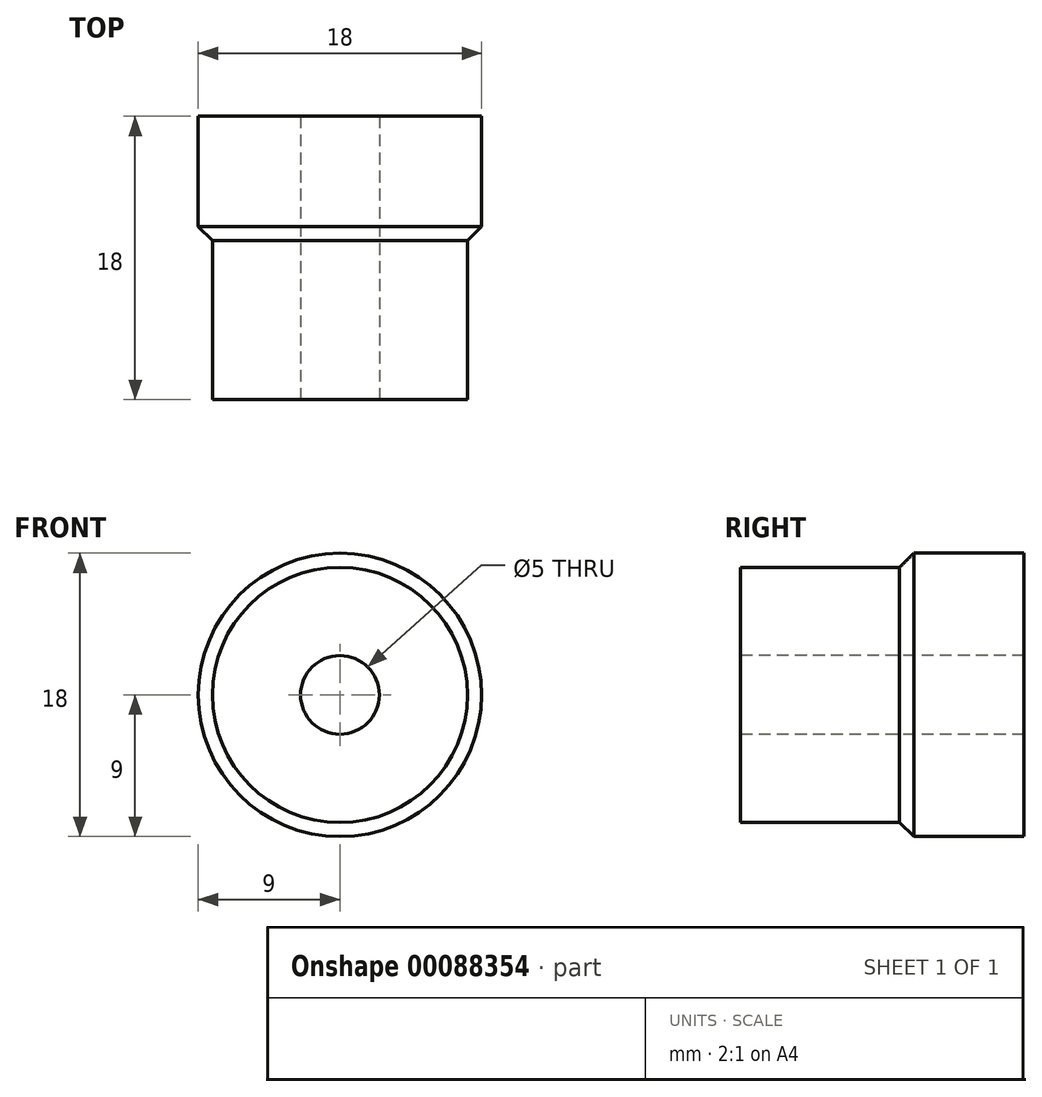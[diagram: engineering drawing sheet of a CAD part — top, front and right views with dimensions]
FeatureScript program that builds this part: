
annotation { "Feature Type Name" : "Feature", "Feature Type Description" : "" }
export const myFeature = defineFeature(function(context is Context, id is Id, definition is map)
    precondition{}
    {
        {
            var Q0;
            Q0=qCreatedBy(makeId("Front.planeOp"),FACE);
            var sketch = newSketch(context, id + "F0", { "sketchPlane" : qUnion([Q0])});
            skCircle(sketch, "E0", {"center": v(0, 0) * mm, "radius": 9 * mm});
            skSolve(sketch);
        }
        {
            var Q0;
            Q0 = qSketchRegion(id + "F0", true);
            extrude(context, id + "F1", {"entities" : qUnion([Q0]), "depth" : 8 * mm});
        }
        {
            var Q0;
            Q0=makeQuery(id+"F1.opExtrude","CAP_FACE",FACE,{"disambiguationData":[OSD([sQuery(id+"F0.wireOp",EDGE,"E0")])],"isStart":false});
            var sketch = newSketch(context, id + "F2", { "sketchPlane" : qUnion([Q0])});
            skCircle(sketch, "E1", {"center": v(0, 0) * mm, "radius": 8.1 * mm});
            skSolve(sketch);
        }
        {
            var Q0;
            Q0 = qSketchRegion(id + "F2", true);
            extrude(context, id + "F3", {"entities" : qUnion([Q0]), "operationType" : NewBodyOperationType.ADD, "depth" : 10 * mm});
        }
        {
            var Q0;
            Q0=makeQuery(id+"F1.opExtrude","CAP_EDGE",EDGE,{"disambiguationData":[OSD([sQuery(id+"F0.wireOp",EDGE,"E0")])],"isStart":false});
            chamfer(context, id + "F4", {"entities" : qUnion([Q0]), "width" : 1 * mm, "tangentPropagation" : true});
        }
        {
            var Q0;
            Q0=makeQuery(id+"F3.opExtrude","CAP_FACE",FACE,{"disambiguationData":[OSD([sQuery(id+"F2.wireOp",EDGE,"E1")])],"isStart":false});
            var sketch = newSketch(context, id + "F5", { "sketchPlane" : qUnion([Q0])});
            skCircle(sketch, "E2", {"center": v(0, 0) * mm, "radius": 2.5 * mm});
            skSolve(sketch);
        }
        {
            var Q0;
            Q0 = qSketchRegion(id + "F5", true);
            extrude(context, id + "F6", {"entities" : qUnion([Q0]), "operationType" : NewBodyOperationType.REMOVE, "endBound" : BoundingType.THROUGH_ALL, "oppositeDirection" : true, "depth" : 25 * mm});
        }
    });
